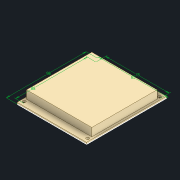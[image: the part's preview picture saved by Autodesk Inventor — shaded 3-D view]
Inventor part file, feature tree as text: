
AUTODESK INVENTOR PART (.ipt)
format: ipt  version: 2022 (Build 260153000, 153)  size: 101,376 bytes
history: native  units: mm
features: sketch x2, extrude x2, hole x1
ambient origin geometry x8: Origin, YZ Plane, XZ Plane, XY Plane, X Axis, Y Axis, Z Axis, Center Point
bodies: Solid1 (feature_tree)
feature tree (5):
  sketch  "Sketch1"  dims[d0=85.0mm d1=98.0mm]
  extrude  "Extrusion1"  Depth=98.0mm
  hole  "Hole1"  [1 undecoded]
  extrude  "Extrusion2"  Depth=2.0mm TaperAngle=0.0deg
  sketch  "Sketch2"  dims[d2=78.0mm d3=88.0mm d4=2.0mm d5=0.0mm d6=3.6mm d7=6.0mm d8=6.5mm d9=3.4mm d10=90.0deg d11=8.0mm d12=20.594885mm d13=80.0mm d14=80.0mm d15=10.0mm d16=0.0mm]
note: 1 required parameter value undecoded (feature->parameter linkage not recoverable at this tier; creation-order binding heuristic only, values carry confidence <= 0.55)
